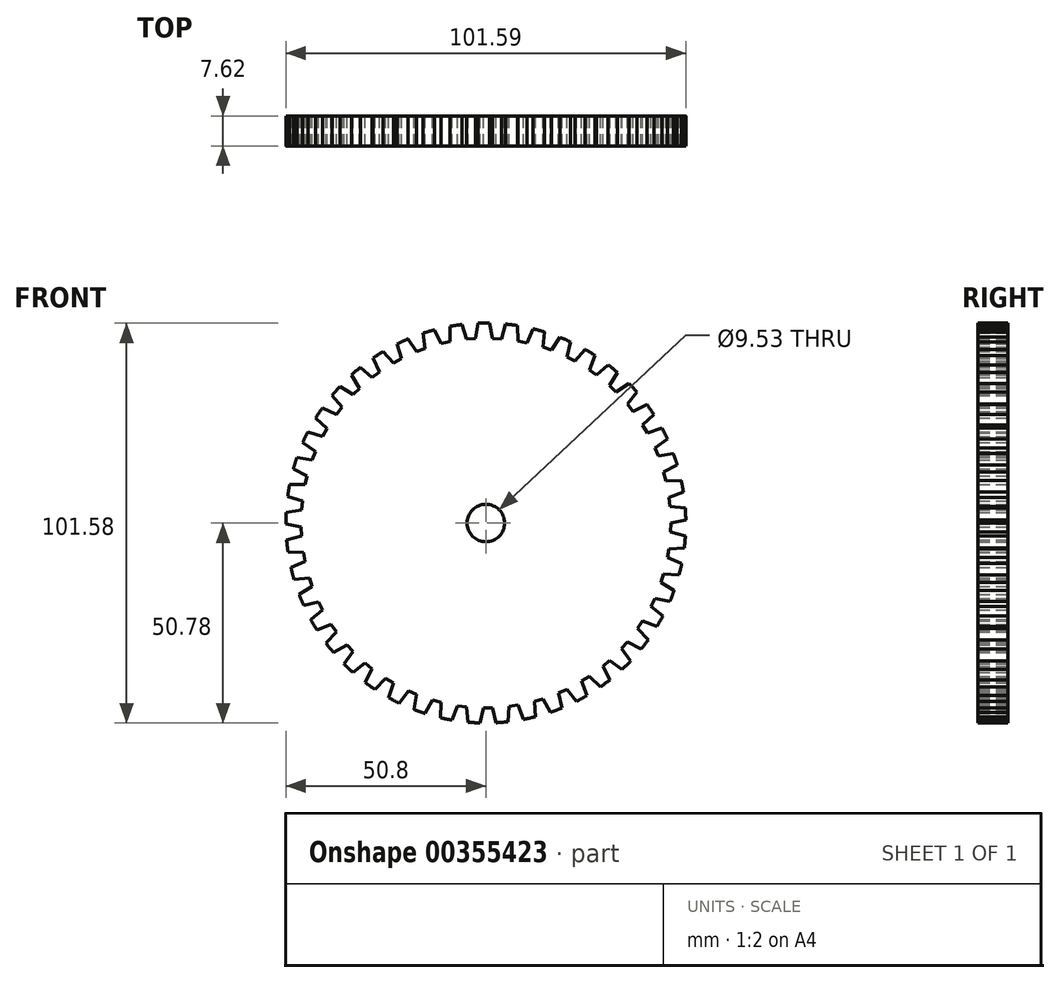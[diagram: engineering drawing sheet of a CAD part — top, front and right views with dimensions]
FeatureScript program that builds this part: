
annotation { "Feature Type Name" : "Feature", "Feature Type Description" : "" }
export const myFeature = defineFeature(function(context is Context, id is Id, definition is map)
    precondition{}
    {
        {
            var Q0;
            Q0=qCreatedBy(makeId("Front.planeOp"),FACE);
            var sketch = newSketch(context, id + "F0", { "sketchPlane" : qUnion([Q0])});
            skCircle(sketch, "E0", {"center": v(0, 0) * mm, "radius": 50.8 * mm});
            skLineSegment(sketch, "E1", {"start": v(-13.06, 49.1) * mm, "end": v(-9.1, 49.98) * mm});
            skLineSegment(sketch, "E2", {"start": v(-13.06, 49.1) * mm, "end": v(-11.36, 45.57) * mm});
            skLineSegment(sketch, "E3", {"start": v(-11.36, 45.57) * mm, "end": v(-9.13, 46.07) * mm});
            skLineSegment(sketch, "E4", {"start": v(-9.13, 46.07) * mm, "end": v(-9.1, 49.98) * mm});
            skLineSegment(sketch, "E5", {"start": v(-10.24, 45.82) * mm, "end": v(-11.08, 49.54) * mm, "construction": true});
            skLineSegment(sketch, "E6.1.0", {"start": v(-19.76, 46.8) * mm, "end": v(-15.96, 48.23) * mm});
            skLineSegment(sketch, "E6.1.1", {"start": v(-19.76, 46.8) * mm, "end": v(-17.6, 43.54) * mm});
            skLineSegment(sketch, "E6.1.2", {"start": v(-15.45, 44.35) * mm, "end": v(-15.96, 48.23) * mm});
            skLineSegment(sketch, "E6.1.3", {"start": v(-16.52, 43.95) * mm, "end": v(-17.86, 47.51) * mm, "construction": true});
            skLineSegment(sketch, "E6.1.4", {"start": v(-17.6, 43.54) * mm, "end": v(-15.45, 44.35) * mm});
            skLineSegment(sketch, "E6.2.0", {"start": v(-26.08, 43.6) * mm, "end": v(-22.52, 45.54) * mm});
            skLineSegment(sketch, "E6.2.1", {"start": v(-26.08, 43.6) * mm, "end": v(-23.48, 40.67) * mm});
            skLineSegment(sketch, "E6.2.2", {"start": v(-21.47, 41.77) * mm, "end": v(-22.52, 45.54) * mm});
            skLineSegment(sketch, "E6.2.3", {"start": v(-22.48, 41.22) * mm, "end": v(-24.3, 44.56) * mm, "construction": true});
            skLineSegment(sketch, "E6.2.4", {"start": v(-23.48, 40.67) * mm, "end": v(-21.47, 41.77) * mm});
            skLineSegment(sketch, "E6.3.0", {"start": v(-31.9, 39.54) * mm, "end": v(-28.64, 41.96) * mm});
            skLineSegment(sketch, "E6.3.1", {"start": v(-31.9, 39.54) * mm, "end": v(-28.91, 37) * mm});
            skLineSegment(sketch, "E6.3.2", {"start": v(-27.08, 38.37) * mm, "end": v(-28.64, 41.96) * mm});
            skLineSegment(sketch, "E6.3.3", {"start": v(-28, 37.7) * mm, "end": v(-30.27, 40.75) * mm, "construction": true});
            skLineSegment(sketch, "E6.3.4", {"start": v(-28.91, 37) * mm, "end": v(-27.08, 38.37) * mm});
            skLineSegment(sketch, "E6.4.0", {"start": v(-37.09, 34.71) * mm, "end": v(-34.2, 37.57) * mm});
            skLineSegment(sketch, "E6.4.1", {"start": v(-37.09, 34.71) * mm, "end": v(-33.78, 32.62) * mm});
            skLineSegment(sketch, "E6.4.2", {"start": v(-32.15, 34.23) * mm, "end": v(-34.2, 37.57) * mm});
            skLineSegment(sketch, "E6.4.3", {"start": v(-32.97, 33.43) * mm, "end": v(-35.64, 36.14) * mm, "construction": true});
            skLineSegment(sketch, "E6.4.4", {"start": v(-33.78, 32.62) * mm, "end": v(-32.15, 34.23) * mm});
            skLineSegment(sketch, "E6.5.0", {"start": v(-41.56, 29.21) * mm, "end": v(-39.1, 32.44) * mm});
            skLineSegment(sketch, "E6.5.1", {"start": v(-41.56, 29.21) * mm, "end": v(-38, 27.6) * mm});
            skLineSegment(sketch, "E6.5.2", {"start": v(-36.6, 29.42) * mm, "end": v(-39.1, 32.44) * mm});
            skLineSegment(sketch, "E6.5.3", {"start": v(-37.3, 28.51) * mm, "end": v(-40.33, 30.83) * mm, "construction": true});
            skLineSegment(sketch, "E6.5.4", {"start": v(-38, 27.6) * mm, "end": v(-36.6, 29.42) * mm});
            skLineSegment(sketch, "E6.6.0", {"start": v(-45.22, 23.15) * mm, "end": v(-43.23, 26.69) * mm});
            skLineSegment(sketch, "E6.6.1", {"start": v(-45.22, 23.15) * mm, "end": v(-41.47, 22.05) * mm});
            skLineSegment(sketch, "E6.6.2", {"start": v(-40.34, 24.04) * mm, "end": v(-43.23, 26.69) * mm});
            skLineSegment(sketch, "E6.6.3", {"start": v(-40.9, 23.05) * mm, "end": v(-44.22, 24.92) * mm, "construction": true});
            skLineSegment(sketch, "E6.6.4", {"start": v(-41.47, 22.05) * mm, "end": v(-40.34, 24.04) * mm});
            skLineSegment(sketch, "E6.7.0", {"start": v(-48, 16.63) * mm, "end": v(-46.52, 20.41) * mm});
            skLineSegment(sketch, "E6.7.1", {"start": v(-48, 16.63) * mm, "end": v(-44.13, 16.06) * mm});
            skLineSegment(sketch, "E6.7.2", {"start": v(-43.3, 18.2) * mm, "end": v(-46.52, 20.41) * mm});
            skLineSegment(sketch, "E6.7.3", {"start": v(-43.71, 17.13) * mm, "end": v(-47.26, 18.52) * mm, "construction": true});
            skLineSegment(sketch, "E6.7.4", {"start": v(-44.13, 16.06) * mm, "end": v(-43.3, 18.2) * mm});
            skLineSegment(sketch, "E6.8.0", {"start": v(-49.85, 9.78) * mm, "end": v(-48.9, 13.74) * mm});
            skLineSegment(sketch, "E6.8.1", {"start": v(-49.85, 9.78) * mm, "end": v(-45.94, 9.77) * mm});
            skLineSegment(sketch, "E6.8.2", {"start": v(-45.4, 11.99) * mm, "end": v(-48.9, 13.74) * mm});
            skLineSegment(sketch, "E6.8.3", {"start": v(-45.67, 10.88) * mm, "end": v(-49.38, 11.76) * mm, "construction": true});
            skLineSegment(sketch, "E6.8.4", {"start": v(-45.94, 9.77) * mm, "end": v(-45.4, 11.99) * mm});
            skLineSegment(sketch, "E6.9.0", {"start": v(-50.73, 2.75) * mm, "end": v(-50.34, 6.8) * mm});
            skLineSegment(sketch, "E6.9.1", {"start": v(-50.73, 2.75) * mm, "end": v(-46.85, 3.28) * mm});
            skLineSegment(sketch, "E6.9.2", {"start": v(-46.63, 5.55) * mm, "end": v(-50.34, 6.8) * mm});
            skLineSegment(sketch, "E6.9.3", {"start": v(-46.74, 4.42) * mm, "end": v(-50.53, 4.77) * mm, "construction": true});
            skLineSegment(sketch, "E6.9.4", {"start": v(-46.85, 3.28) * mm, "end": v(-46.63, 5.55) * mm});
            skLineSegment(sketch, "E6.10.0", {"start": v(-50.61, -4.34) * mm, "end": v(-50.8, -0.28) * mm});
            skLineSegment(sketch, "E6.10.1", {"start": v(-50.61, -4.34) * mm, "end": v(-46.85, -3.27) * mm});
            skLineSegment(sketch, "E6.10.2", {"start": v(-46.95, -1) * mm, "end": v(-50.8, -0.28) * mm});
            skLineSegment(sketch, "E6.10.3", {"start": v(-46.9, -2.13) * mm, "end": v(-50.7, -2.3) * mm, "construction": true});
            skLineSegment(sketch, "E6.10.4", {"start": v(-46.85, -3.27) * mm, "end": v(-46.95, -1) * mm});
            skLineSegment(sketch, "E6.11.0", {"start": v(-49.52, -11.34) * mm, "end": v(-50.27, -7.34) * mm});
            skLineSegment(sketch, "E6.11.1", {"start": v(-49.52, -11.34) * mm, "end": v(-45.94, -9.76) * mm});
            skLineSegment(sketch, "E6.11.2", {"start": v(-46.36, -7.52) * mm, "end": v(-50.27, -7.34) * mm});
            skLineSegment(sketch, "E6.11.3", {"start": v(-46.15, -8.64) * mm, "end": v(-49.9, -9.34) * mm, "construction": true});
            skLineSegment(sketch, "E6.11.4", {"start": v(-45.94, -9.76) * mm, "end": v(-46.36, -7.52) * mm});
            skLineSegment(sketch, "E6.12.0", {"start": v(-47.46, -18.12) * mm, "end": v(-48.76, -14.27) * mm});
            skLineSegment(sketch, "E6.12.1", {"start": v(-47.46, -18.12) * mm, "end": v(-44.13, -16.06) * mm});
            skLineSegment(sketch, "E6.12.2", {"start": v(-44.86, -13.9) * mm, "end": v(-48.76, -14.27) * mm});
            skLineSegment(sketch, "E6.12.3", {"start": v(-44.5, -14.98) * mm, "end": v(-48.1, -16.2) * mm, "construction": true});
            skLineSegment(sketch, "E6.12.4", {"start": v(-44.13, -16.06) * mm, "end": v(-44.86, -13.9) * mm});
            skLineSegment(sketch, "E6.13.0", {"start": v(-44.48, -24.55) * mm, "end": v(-46.3, -20.91) * mm});
            skLineSegment(sketch, "E6.13.1", {"start": v(-44.48, -24.55) * mm, "end": v(-41.47, -22.05) * mm});
            skLineSegment(sketch, "E6.13.2", {"start": v(-42.5, -20) * mm, "end": v(-46.3, -20.91) * mm});
            skLineSegment(sketch, "E6.13.3", {"start": v(-41.98, -21.02) * mm, "end": v(-45.39, -22.73) * mm, "construction": true});
            skLineSegment(sketch, "E6.13.4", {"start": v(-41.47, -22.05) * mm, "end": v(-42.5, -20) * mm});
            skLineSegment(sketch, "E6.14.0", {"start": v(-40.63, -30.5) * mm, "end": v(-42.93, -27.15) * mm});
            skLineSegment(sketch, "E6.14.1", {"start": v(-40.63, -30.5) * mm, "end": v(-38, -27.6) * mm});
            skLineSegment(sketch, "E6.14.2", {"start": v(-39.3, -25.72) * mm, "end": v(-42.93, -27.15) * mm});
            skLineSegment(sketch, "E6.14.3", {"start": v(-38.64, -26.66) * mm, "end": v(-41.78, -28.83) * mm, "construction": true});
            skLineSegment(sketch, "E6.14.4", {"start": v(-38, -27.6) * mm, "end": v(-39.3, -25.72) * mm});
            skLineSegment(sketch, "E6.15.0", {"start": v(-35.99, -35.86) * mm, "end": v(-38.74, -32.86) * mm});
            skLineSegment(sketch, "E6.15.1", {"start": v(-35.99, -35.86) * mm, "end": v(-33.78, -32.62) * mm});
            skLineSegment(sketch, "E6.15.2", {"start": v(-35.33, -30.94) * mm, "end": v(-38.74, -32.86) * mm});
            skLineSegment(sketch, "E6.15.3", {"start": v(-34.56, -31.78) * mm, "end": v(-37.36, -34.36) * mm, "construction": true});
            skLineSegment(sketch, "E6.15.4", {"start": v(-33.78, -32.62) * mm, "end": v(-35.33, -30.94) * mm});
            skLineSegment(sketch, "E6.16.0", {"start": v(-30.65, -40.51) * mm, "end": v(-33.79, -37.94) * mm});
            skLineSegment(sketch, "E6.16.1", {"start": v(-30.65, -40.51) * mm, "end": v(-28.91, -37) * mm});
            skLineSegment(sketch, "E6.16.2", {"start": v(-30.68, -35.56) * mm, "end": v(-33.79, -37.94) * mm});
            skLineSegment(sketch, "E6.16.3", {"start": v(-29.8, -36.28) * mm, "end": v(-32.22, -39.23) * mm, "construction": true});
            skLineSegment(sketch, "E6.16.4", {"start": v(-28.91, -37) * mm, "end": v(-30.68, -35.56) * mm});
            skLineSegment(sketch, "E6.17.0", {"start": v(-24.7, -44.39) * mm, "end": v(-28.18, -42.27) * mm});
            skLineSegment(sketch, "E6.17.1", {"start": v(-24.7, -44.39) * mm, "end": v(-23.48, -40.67) * mm});
            skLineSegment(sketch, "E6.17.2", {"start": v(-25.43, -39.48) * mm, "end": v(-28.18, -42.27) * mm});
            skLineSegment(sketch, "E6.17.3", {"start": v(-24.46, -40.08) * mm, "end": v(-26.44, -43.33) * mm, "construction": true});
            skLineSegment(sketch, "E6.17.4", {"start": v(-23.48, -40.67) * mm, "end": v(-25.43, -39.48) * mm});
            skLineSegment(sketch, "E6.18.0", {"start": v(-18.3, -47.4) * mm, "end": v(-22.02, -45.78) * mm});
            skLineSegment(sketch, "E6.18.1", {"start": v(-18.3, -47.4) * mm, "end": v(-17.6, -43.54) * mm});
            skLineSegment(sketch, "E6.18.2", {"start": v(-19.7, -42.64) * mm, "end": v(-22.02, -45.78) * mm});
            skLineSegment(sketch, "E6.18.3", {"start": v(-18.64, -43.09) * mm, "end": v(-20.16, -46.59) * mm, "construction": true});
            skLineSegment(sketch, "E6.18.4", {"start": v(-17.6, -43.54) * mm, "end": v(-19.7, -42.64) * mm});
            skLineSegment(sketch, "E6.19.0", {"start": v(-11.52, -49.48) * mm, "end": v(-15.44, -48.4) * mm});
            skLineSegment(sketch, "E6.19.1", {"start": v(-11.52, -49.48) * mm, "end": v(-11.36, -45.57) * mm});
            skLineSegment(sketch, "E6.19.2", {"start": v(-13.57, -44.96) * mm, "end": v(-15.44, -48.4) * mm});
            skLineSegment(sketch, "E6.19.3", {"start": v(-12.47, -45.26) * mm, "end": v(-13.48, -48.94) * mm, "construction": true});
            skLineSegment(sketch, "E6.19.4", {"start": v(-11.36, -45.57) * mm, "end": v(-13.57, -44.96) * mm});
            skLineSegment(sketch, "E6.20.0", {"start": v(-4.52, -50.6) * mm, "end": v(-8.55, -50.08) * mm});
            skLineSegment(sketch, "E6.20.1", {"start": v(-4.52, -50.6) * mm, "end": v(-4.91, -46.7) * mm});
            skLineSegment(sketch, "E6.20.2", {"start": v(-7.18, -46.41) * mm, "end": v(-8.55, -50.08) * mm});
            skLineSegment(sketch, "E6.20.3", {"start": v(-6.04, -46.56) * mm, "end": v(-6.53, -50.34) * mm, "construction": true});
            skLineSegment(sketch, "E6.20.4", {"start": v(-4.91, -46.7) * mm, "end": v(-7.18, -46.41) * mm});
            skLineSegment(sketch, "E6.21.0", {"start": v(2.57, -50.74) * mm, "end": v(-1.5, -50.78) * mm});
            skLineSegment(sketch, "E6.21.1", {"start": v(2.57, -50.74) * mm, "end": v(1.64, -46.93) * mm});
            skLineSegment(sketch, "E6.21.2", {"start": v(-0.65, -46.96) * mm, "end": v(-1.5, -50.78) * mm});
            skLineSegment(sketch, "E6.21.3", {"start": v(0.5, -46.95) * mm, "end": v(0.53, -50.76) * mm, "construction": true});
            skLineSegment(sketch, "E6.21.4", {"start": v(1.64, -46.93) * mm, "end": v(-0.65, -46.96) * mm});
            skLineSegment(sketch, "E6.22.0", {"start": v(9.6, -49.88) * mm, "end": v(5.58, -50.5) * mm});
            skLineSegment(sketch, "E6.22.1", {"start": v(9.6, -49.88) * mm, "end": v(8.15, -46.25) * mm});
            skLineSegment(sketch, "E6.22.2", {"start": v(5.9, -46.6) * mm, "end": v(5.58, -50.5) * mm});
            skLineSegment(sketch, "E6.22.3", {"start": v(7.02, -46.42) * mm, "end": v(7.6, -50.19) * mm, "construction": true});
            skLineSegment(sketch, "E6.22.4", {"start": v(8.15, -46.25) * mm, "end": v(5.9, -46.6) * mm});
            skLineSegment(sketch, "E6.23.0", {"start": v(16.45, -48.06) * mm, "end": v(12.56, -49.22) * mm});
            skLineSegment(sketch, "E6.23.1", {"start": v(16.45, -48.06) * mm, "end": v(14.51, -44.67) * mm});
            skLineSegment(sketch, "E6.23.2", {"start": v(12.32, -45.32) * mm, "end": v(12.56, -49.22) * mm});
            skLineSegment(sketch, "E6.23.3", {"start": v(13.42, -45) * mm, "end": v(14.5, -48.64) * mm, "construction": true});
            skLineSegment(sketch, "E6.23.4", {"start": v(14.51, -44.67) * mm, "end": v(12.32, -45.32) * mm});
            skLineSegment(sketch, "E6.24.0", {"start": v(22.98, -45.3) * mm, "end": v(19.29, -47) * mm});
            skLineSegment(sketch, "E6.24.1", {"start": v(22.98, -45.3) * mm, "end": v(20.59, -42.21) * mm});
            skLineSegment(sketch, "E6.24.2", {"start": v(18.5, -43.16) * mm, "end": v(19.29, -47) * mm});
            skLineSegment(sketch, "E6.24.3", {"start": v(19.55, -42.69) * mm, "end": v(21.13, -46.15) * mm, "construction": true});
            skLineSegment(sketch, "E6.24.4", {"start": v(20.59, -42.21) * mm, "end": v(18.5, -43.16) * mm});
            skLineSegment(sketch, "E6.25.0", {"start": v(29.06, -41.67) * mm, "end": v(25.64, -43.86) * mm});
            skLineSegment(sketch, "E6.25.1", {"start": v(29.06, -41.67) * mm, "end": v(26.26, -38.94) * mm});
            skLineSegment(sketch, "E6.25.2", {"start": v(24.33, -40.17) * mm, "end": v(25.64, -43.86) * mm});
            skLineSegment(sketch, "E6.25.3", {"start": v(25.3, -39.55) * mm, "end": v(27.35, -42.76) * mm, "construction": true});
            skLineSegment(sketch, "E6.25.4", {"start": v(26.26, -38.94) * mm, "end": v(24.33, -40.17) * mm});
            skLineSegment(sketch, "E6.26.0", {"start": v(34.58, -37.22) * mm, "end": v(31.5, -39.86) * mm});
            skLineSegment(sketch, "E6.26.1", {"start": v(34.58, -37.22) * mm, "end": v(31.42, -34.9) * mm});
            skLineSegment(sketch, "E6.26.2", {"start": v(29.69, -36.39) * mm, "end": v(31.5, -39.86) * mm});
            skLineSegment(sketch, "E6.26.3", {"start": v(30.56, -35.65) * mm, "end": v(33.04, -38.54) * mm, "construction": true});
            skLineSegment(sketch, "E6.26.4", {"start": v(31.42, -34.9) * mm, "end": v(29.69, -36.39) * mm});
            skLineSegment(sketch, "E6.27.0", {"start": v(39.42, -32.04) * mm, "end": v(36.73, -35.09) * mm});
            skLineSegment(sketch, "E6.27.1", {"start": v(39.42, -32.04) * mm, "end": v(35.97, -30.19) * mm});
            skLineSegment(sketch, "E6.27.2", {"start": v(34.46, -31.9) * mm, "end": v(36.73, -35.09) * mm});
            skLineSegment(sketch, "E6.27.3", {"start": v(35.22, -31.05) * mm, "end": v(38.08, -33.57) * mm, "construction": true});
            skLineSegment(sketch, "E6.27.4", {"start": v(35.97, -30.19) * mm, "end": v(34.46, -31.9) * mm});
            skLineSegment(sketch, "E6.28.0", {"start": v(43.5, -26.24) * mm, "end": v(41.26, -29.64) * mm});
            skLineSegment(sketch, "E6.28.1", {"start": v(43.5, -26.24) * mm, "end": v(39.83, -24.89) * mm});
            skLineSegment(sketch, "E6.28.2", {"start": v(38.57, -26.8) * mm, "end": v(41.26, -29.64) * mm});
            skLineSegment(sketch, "E6.28.3", {"start": v(39.2, -25.84) * mm, "end": v(42.38, -27.94) * mm, "construction": true});
            skLineSegment(sketch, "E6.28.4", {"start": v(39.83, -24.89) * mm, "end": v(38.57, -26.8) * mm});
            skLineSegment(sketch, "E6.29.0", {"start": v(46.73, -19.93) * mm, "end": v(44.98, -23.6) * mm});
            skLineSegment(sketch, "E6.29.1", {"start": v(46.73, -19.93) * mm, "end": v(42.9, -19.1) * mm});
            skLineSegment(sketch, "E6.29.2", {"start": v(41.92, -21.17) * mm, "end": v(44.98, -23.6) * mm});
            skLineSegment(sketch, "E6.29.3", {"start": v(42.41, -20.14) * mm, "end": v(45.85, -21.77) * mm, "construction": true});
            skLineSegment(sketch, "E6.29.4", {"start": v(42.9, -19.1) * mm, "end": v(41.92, -21.17) * mm});
            skLineSegment(sketch, "E6.30.0", {"start": v(49.05, -13.24) * mm, "end": v(47.83, -17.12) * mm});
            skLineSegment(sketch, "E6.30.1", {"start": v(49.05, -13.24) * mm, "end": v(45.14, -12.95) * mm});
            skLineSegment(sketch, "E6.30.2", {"start": v(44.46, -15.13) * mm, "end": v(47.83, -17.12) * mm});
            skLineSegment(sketch, "E6.30.3", {"start": v(44.8, -14.04) * mm, "end": v(48.44, -15.18) * mm, "construction": true});
            skLineSegment(sketch, "E6.30.4", {"start": v(45.14, -12.95) * mm, "end": v(44.46, -15.13) * mm});
            skLineSegment(sketch, "E6.31.0", {"start": v(50.4, -6.28) * mm, "end": v(49.75, -10.3) * mm});
            skLineSegment(sketch, "E6.31.1", {"start": v(50.4, -6.28) * mm, "end": v(46.5, -6.54) * mm});
            skLineSegment(sketch, "E6.31.2", {"start": v(46.13, -8.8) * mm, "end": v(49.75, -10.3) * mm});
            skLineSegment(sketch, "E6.31.3", {"start": v(46.32, -7.67) * mm, "end": v(50.08, -8.29) * mm, "construction": true});
            skLineSegment(sketch, "E6.31.4", {"start": v(46.5, -6.54) * mm, "end": v(46.13, -8.8) * mm});
            skLineSegment(sketch, "E6.32.0", {"start": v(50.8, 0.8) * mm, "end": v(50.7, -3.27) * mm});
            skLineSegment(sketch, "E6.32.1", {"start": v(50.8, 0.8) * mm, "end": v(46.96, 0) * mm});
            skLineSegment(sketch, "E6.32.2", {"start": v(46.9, -2.29) * mm, "end": v(50.7, -3.27) * mm});
            skLineSegment(sketch, "E6.32.3", {"start": v(46.94, -1.14) * mm, "end": v(50.74, -1.24) * mm, "construction": true});
            skLineSegment(sketch, "E6.32.4", {"start": v(46.96, 0) * mm, "end": v(46.9, -2.29) * mm});
            skLineSegment(sketch, "E6.33.0", {"start": v(50.19, 7.86) * mm, "end": v(50.66, 3.82) * mm});
            skLineSegment(sketch, "E6.33.1", {"start": v(50.19, 7.86) * mm, "end": v(46.5, 6.53) * mm});
            skLineSegment(sketch, "E6.33.2", {"start": v(46.77, 4.26) * mm, "end": v(50.66, 3.82) * mm});
            skLineSegment(sketch, "E6.33.3", {"start": v(46.64, 5.4) * mm, "end": v(50.42, 5.84) * mm, "construction": true});
            skLineSegment(sketch, "E6.33.4", {"start": v(46.5, 6.53) * mm, "end": v(46.77, 4.26) * mm});
            skLineSegment(sketch, "E6.34.0", {"start": v(48.6, 14.76) * mm, "end": v(49.63, 10.83) * mm});
            skLineSegment(sketch, "E6.34.1", {"start": v(48.6, 14.76) * mm, "end": v(45.14, 12.94) * mm});
            skLineSegment(sketch, "E6.34.2", {"start": v(45.72, 10.73) * mm, "end": v(49.63, 10.83) * mm});
            skLineSegment(sketch, "E6.34.3", {"start": v(45.43, 11.84) * mm, "end": v(49.12, 12.8) * mm, "construction": true});
            skLineSegment(sketch, "E6.34.4", {"start": v(45.14, 12.94) * mm, "end": v(45.72, 10.73) * mm});
            skLineSegment(sketch, "E6.35.0", {"start": v(46.08, 21.39) * mm, "end": v(47.64, 17.63) * mm});
            skLineSegment(sketch, "E6.35.1", {"start": v(46.08, 21.39) * mm, "end": v(42.9, 19.1) * mm});
            skLineSegment(sketch, "E6.35.2", {"start": v(43.78, 16.99) * mm, "end": v(47.64, 17.63) * mm});
            skLineSegment(sketch, "E6.35.3", {"start": v(43.34, 18.04) * mm, "end": v(46.86, 19.5) * mm, "construction": true});
            skLineSegment(sketch, "E6.35.4", {"start": v(42.9, 19.1) * mm, "end": v(43.78, 16.99) * mm});
            skLineSegment(sketch, "E6.36.0", {"start": v(42.65, 27.6) * mm, "end": v(44.72, 24.1) * mm});
            skLineSegment(sketch, "E6.36.1", {"start": v(42.65, 27.6) * mm, "end": v(39.83, 24.89) * mm});
            skLineSegment(sketch, "E6.36.2", {"start": v(41, 22.92) * mm, "end": v(44.72, 24.1) * mm});
            skLineSegment(sketch, "E6.36.3", {"start": v(40.4, 23.9) * mm, "end": v(43.69, 25.84) * mm, "construction": true});
            skLineSegment(sketch, "E6.36.4", {"start": v(39.83, 24.89) * mm, "end": v(41, 22.92) * mm});
            skLineSegment(sketch, "E6.37.0", {"start": v(38.4, 33.26) * mm, "end": v(40.94, 30.08) * mm});
            skLineSegment(sketch, "E6.37.1", {"start": v(38.4, 33.26) * mm, "end": v(35.98, 30.19) * mm});
            skLineSegment(sketch, "E6.37.2", {"start": v(37.4, 28.4) * mm, "end": v(40.94, 30.08) * mm});
            skLineSegment(sketch, "E6.37.3", {"start": v(36.7, 29.3) * mm, "end": v(39.67, 31.67) * mm, "construction": true});
            skLineSegment(sketch, "E6.37.4", {"start": v(35.98, 30.19) * mm, "end": v(37.4, 28.4) * mm});
            skLineSegment(sketch, "E6.38.0", {"start": v(33.4, 38.28) * mm, "end": v(36.35, 35.49) * mm});
            skLineSegment(sketch, "E6.38.1", {"start": v(33.4, 38.28) * mm, "end": v(31.43, 34.9) * mm});
            skLineSegment(sketch, "E6.38.2", {"start": v(33.09, 33.33) * mm, "end": v(36.35, 35.49) * mm});
            skLineSegment(sketch, "E6.38.3", {"start": v(32.26, 34.11) * mm, "end": v(34.87, 36.88) * mm, "construction": true});
            skLineSegment(sketch, "E6.38.4", {"start": v(31.43, 34.9) * mm, "end": v(33.09, 33.33) * mm});
            skLineSegment(sketch, "E6.39.0", {"start": v(27.75, 42.55) * mm, "end": v(31.06, 40.2) * mm});
            skLineSegment(sketch, "E6.39.1", {"start": v(27.75, 42.55) * mm, "end": v(26.26, 38.93) * mm});
            skLineSegment(sketch, "E6.39.2", {"start": v(28.13, 37.6) * mm, "end": v(31.06, 40.2) * mm});
            skLineSegment(sketch, "E6.39.3", {"start": v(27.2, 38.27) * mm, "end": v(29.4, 41.38) * mm, "construction": true});
            skLineSegment(sketch, "E6.39.4", {"start": v(26.26, 38.93) * mm, "end": v(28.13, 37.6) * mm});
            skLineSegment(sketch, "E6.40.0", {"start": v(21.55, 46) * mm, "end": v(25.16, 44.13) * mm});
            skLineSegment(sketch, "E6.40.1", {"start": v(21.55, 46) * mm, "end": v(20.59, 42.2) * mm});
            skLineSegment(sketch, "E6.40.2", {"start": v(22.62, 41.16) * mm, "end": v(25.16, 44.13) * mm});
            skLineSegment(sketch, "E6.40.3", {"start": v(21.6, 41.68) * mm, "end": v(23.36, 45.07) * mm, "construction": true});
            skLineSegment(sketch, "E6.40.4", {"start": v(20.59, 42.2) * mm, "end": v(22.62, 41.16) * mm});
            skLineSegment(sketch, "E6.41.0", {"start": v(14.94, 48.55) * mm, "end": v(18.77, 47.2) * mm});
            skLineSegment(sketch, "E6.41.1", {"start": v(14.94, 48.55) * mm, "end": v(14.51, 44.66) * mm});
            skLineSegment(sketch, "E6.41.2", {"start": v(16.67, 43.9) * mm, "end": v(18.77, 47.2) * mm});
            skLineSegment(sketch, "E6.41.3", {"start": v(15.6, 44.28) * mm, "end": v(16.86, 47.88) * mm, "construction": true});
            skLineSegment(sketch, "E6.41.4", {"start": v(14.51, 44.66) * mm, "end": v(16.67, 43.9) * mm});
            skLineSegment(sketch, "E6.42.0", {"start": v(8.04, 50.16) * mm, "end": v(12.02, 49.36) * mm});
            skLineSegment(sketch, "E6.42.1", {"start": v(8.04, 50.16) * mm, "end": v(8.16, 46.25) * mm});
            skLineSegment(sketch, "E6.42.2", {"start": v(10.4, 45.8) * mm, "end": v(12.02, 49.36) * mm});
            skLineSegment(sketch, "E6.42.3", {"start": v(9.28, 46.02) * mm, "end": v(10.03, 49.76) * mm, "construction": true});
            skLineSegment(sketch, "E6.42.4", {"start": v(8.16, 46.25) * mm, "end": v(10.4, 45.8) * mm});
            skLineSegment(sketch, "E6.43.0", {"start": v(0.98, 50.8) * mm, "end": v(5.04, 50.55) * mm});
            skLineSegment(sketch, "E6.43.1", {"start": v(0.98, 50.8) * mm, "end": v(1.64, 46.93) * mm});
            skLineSegment(sketch, "E6.43.2", {"start": v(3.92, 46.8) * mm, "end": v(5.04, 50.55) * mm});
            skLineSegment(sketch, "E6.43.3", {"start": v(2.78, 46.87) * mm, "end": v(3, 50.67) * mm, "construction": true});
            skLineSegment(sketch, "E6.43.4", {"start": v(1.64, 46.93) * mm, "end": v(3.92, 46.8) * mm});
            skLineSegment(sketch, "E6.44.0", {"start": v(-6.1, 50.43) * mm, "end": v(-2.05, 50.76) * mm});
            skLineSegment(sketch, "E6.44.1", {"start": v(-6.1, 50.43) * mm, "end": v(-4.9, 46.7) * mm});
            skLineSegment(sketch, "E6.44.2", {"start": v(-2.63, 46.89) * mm, "end": v(-2.05, 50.76) * mm});
            skLineSegment(sketch, "E6.44.3", {"start": v(-3.77, 46.8) * mm, "end": v(-4.07, 50.6) * mm, "construction": true});
            skLineSegment(sketch, "E6.44.4", {"start": v(-4.9, 46.7) * mm, "end": v(-2.63, 46.89) * mm});
            skCircle(sketch, "E7", {"center": v(0, 0) * mm, "radius": 4.76 * mm});
            skSolve(sketch);
        }
        {
            var Q0;
            {var subQ43=sQuery(id+"F0.wireOp",EDGE,"E2");Q0=makeQuery(id+"F0.imprint","IMPRINT",FACE,{"disambiguationData":[TD([[makeQuery(id+"F0.imprint","IMPRINT",EDGE,{"derivedFrom":subQ43}),-1.0]])]});}
            extrude(context, id + "F1", {"entities" : qUnion([Q0]), "depth" : 7.62 * mm});
        }
    });
